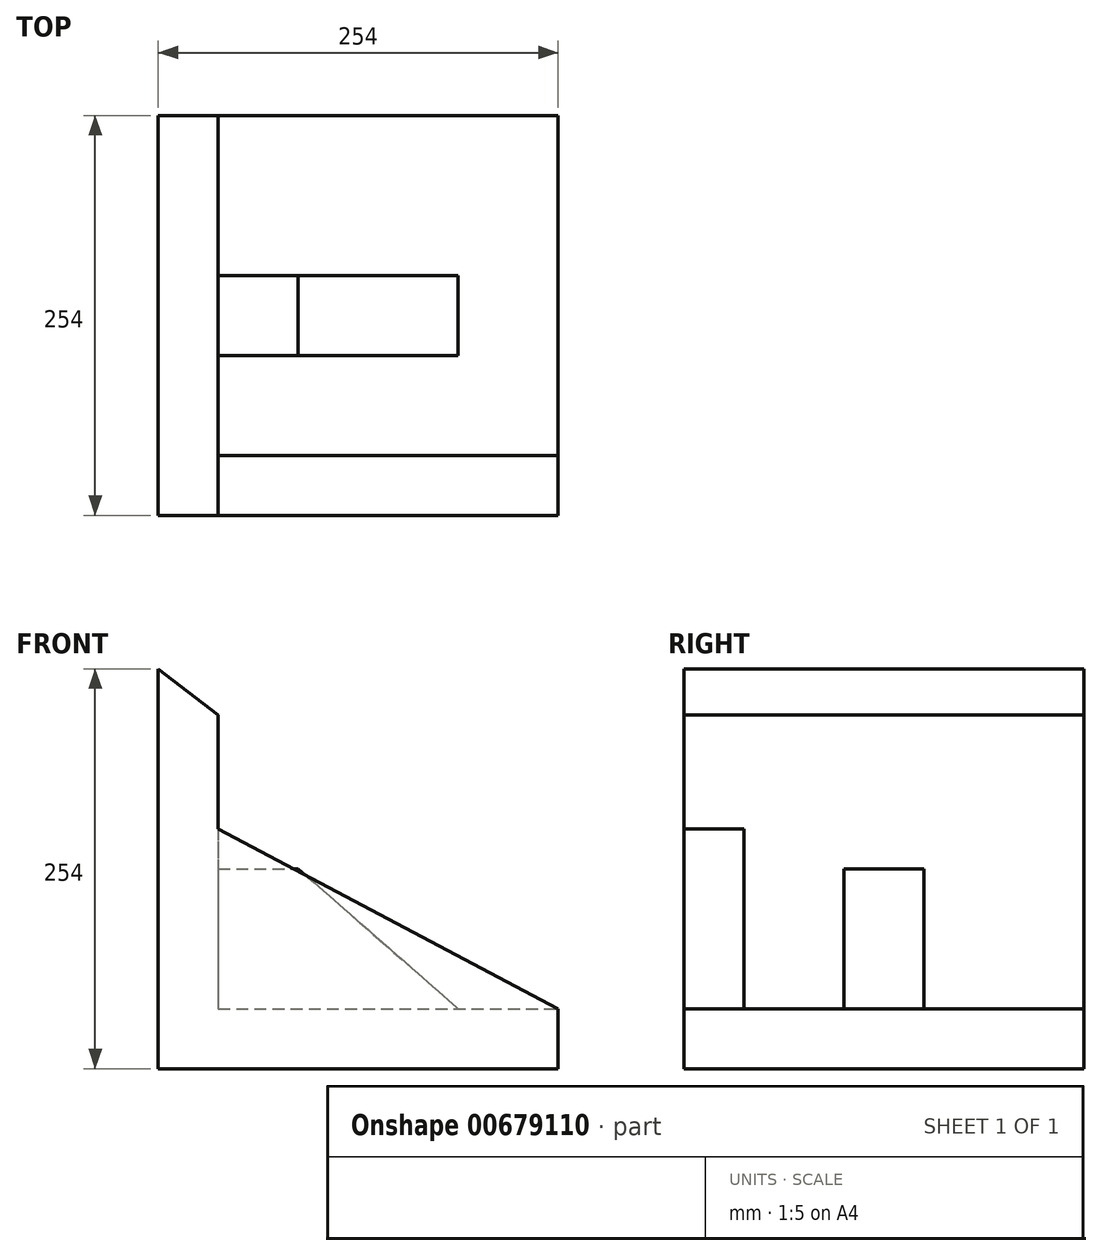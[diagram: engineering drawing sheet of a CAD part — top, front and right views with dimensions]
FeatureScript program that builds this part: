
annotation { "Feature Type Name" : "Feature", "Feature Type Description" : "" }
export const myFeature = defineFeature(function(context is Context, id is Id, definition is map)
    precondition{}
    {
        {
            var Q0;
            Q0=qCreatedBy(makeId("Front.planeOp"),FACE);
            var sketch = newSketch(context, id + "F0", { "sketchPlane" : qUnion([Q0])});
            skLineSegment(sketch, "E0", {"start": v(0, 186.7) * mm, "end": v(0, 0) * mm});
            skLineSegment(sketch, "E1", {"start": v(0, 0) * mm, "end": v(215.9, 0) * mm});
            skLineSegment(sketch, "E2", {"start": v(215.9, 0) * mm, "end": v(215.9, -38.1) * mm});
            skLineSegment(sketch, "E3", {"start": v(215.9, -38.1) * mm, "end": v(-38.1, -38.1) * mm});
            skLineSegment(sketch, "E4", {"start": v(-38.1, -38.1) * mm, "end": v(-38.1, 215.9) * mm});
            skLineSegment(sketch, "E5", {"start": v(-38.1, 215.9) * mm, "end": v(0, 186.69) * mm});
            skLineSegment(sketch, "E6", {"start": v(0, 88.9) * mm, "end": v(50.8, 88.9) * mm});
            skLineSegment(sketch, "E7", {"start": v(50.8, 88.9) * mm, "end": v(152.4, 0) * mm});
            skSolve(sketch);
        }
        {
            var Q0;
            {var subQ0=sQuery(id+"F0.wireOp",EDGE,"E1");Q0=makeQuery(id+"F0.imprint","IMPRINT",FACE,{"disambiguationData":[TD([[makeQuery(id+"F0.imprint","IMPRINT",EDGE,{"derivedFrom":subQ0}),-1.0]])]});}
            extrude(context, id + "F1", {"entities" : qUnion([Q0]), "endBound" : BoundingType.SYMMETRIC, "depth" : 254 * mm, "offsetDistance" : 25.4 * mm});
        }
        {
            var Q0;
            Q0=makeQuery(id+"F1.opExtrude","CAP_FACE",FACE,{"disambiguationData":[OSD([sQuery(id+"F0.wireOp",EDGE,"E0"),sQuery(id+"F0.wireOp",EDGE,"E1"),sQuery(id+"F0.wireOp",EDGE,"E2"),sQuery(id+"F0.wireOp",EDGE,"E3"),sQuery(id+"F0.wireOp",EDGE,"E4"),sQuery(id+"F0.wireOp",EDGE,"E5")])],"isStart":false});
            var sketch = newSketch(context, id + "F2", { "sketchPlane" : qUnion([Q0])});
            skLineSegment(sketch, "E8", {"start": v(0, 114.3) * mm, "end": v(215.9, 0) * mm});
            skSolve(sketch);
        }
        {
            var Q0;
            {var subQ0=sQuery(id+"F2.wireOp",EDGE,"E8");Q0=makeQuery(id+"F2.imprint","IMPRINT",FACE,{"disambiguationData":[TD([[makeQuery(id+"F2.imprint","IMPRINT",EDGE,{"derivedFrom":subQ0}),-1.0]])]});}
            extrude(context, id + "F3", {"entities" : qUnion([Q0]), "operationType" : NewBodyOperationType.ADD, "oppositeDirection" : true, "depth" : 38.1 * mm, "offsetDistance" : 25.4 * mm});
        }
        {
            var Q0;
            Q0 = qSketchRegion(id + "F0", true);
            extrude(context, id + "F4", {"entities" : qUnion([Q0]), "operationType" : NewBodyOperationType.ADD, "endBound" : BoundingType.SYMMETRIC, "depth" : 50.8 * mm, "offsetDistance" : 25.4 * mm});
        }
    });
